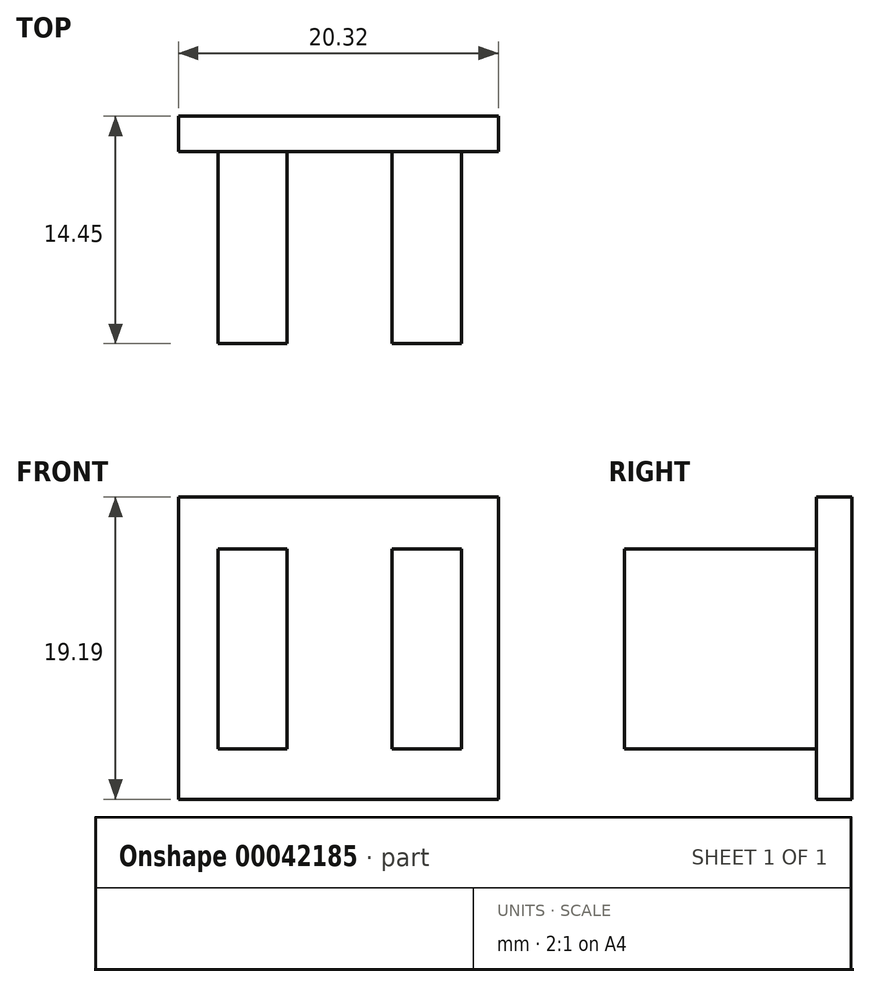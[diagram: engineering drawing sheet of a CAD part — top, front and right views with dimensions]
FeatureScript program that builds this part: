
annotation { "Feature Type Name" : "Feature", "Feature Type Description" : "" }
export const myFeature = defineFeature(function(context is Context, id is Id, definition is map)
    precondition{}
    {
        {
            var Q0;
            Q0=qCreatedBy(makeId("Front.planeOp"),FACE);
            var sketch = newSketch(context, id + "F0", { "sketchPlane" : qUnion([Q0])});
            skLineSegment(sketch, "E0.rect.bottom", {"start": v(0, 1.86) * mm, "end": v(-20.32, 1.86) * mm});
            skLineSegment(sketch, "E0.rect.top", {"start": v(0, 21.05) * mm, "end": v(-20.32, 21.05) * mm});
            skLineSegment(sketch, "E0.rect.left", {"start": v(0, 1.86) * mm, "end": v(0, 21.05) * mm});
            skLineSegment(sketch, "E0.rect.right", {"start": v(-20.32, 1.86) * mm, "end": v(-20.32, 21.05) * mm});
            skPoint(sketch, "E0.rect.middle", {"position": v(-10.16, 11.45) * mm});
            skSolve(sketch);
        }
        {
            var Q0;
            Q0 = qSketchRegion(id + "F0", true);
            extrude(context, id + "F1", {"entities" : qUnion([Q0]), "depth" : 2.26 * mm});
        }
        {
            var Q0;
            Q0=makeQuery(id+"F1.opExtrude","CAP_FACE",FACE,{"disambiguationData":[OSD([sQuery(id+"F0.wireOp",EDGE,"E0.rect.bottom"),sQuery(id+"F0.wireOp",EDGE,"E0.rect.top"),sQuery(id+"F0.wireOp",EDGE,"E0.rect.left"),sQuery(id+"F0.wireOp",EDGE,"E0.rect.right")])],"isStart":false});
            var sketch = newSketch(context, id + "F2", { "sketchPlane" : qUnion([Q0])});
            skLineSegment(sketch, "E1.rect.bottom", {"start": v(-13.42, 5.05) * mm, "end": v(-17.81, 5.05) * mm});
            skLineSegment(sketch, "E1.rect.top", {"start": v(-13.42, 17.75) * mm, "end": v(-17.81, 17.75) * mm});
            skLineSegment(sketch, "E1.rect.left", {"start": v(-13.42, 5.05) * mm, "end": v(-13.42, 17.75) * mm});
            skLineSegment(sketch, "E1.rect.right", {"start": v(-17.81, 5.05) * mm, "end": v(-17.81, 17.75) * mm});
            skPoint(sketch, "E1.rect.middle", {"position": v(-15.61, 11.4) * mm});
            skLineSegment(sketch, "E2", {"start": v(-10.08, -6.85) * mm, "end": v(-10.08, 35.98) * mm, "construction": true});
            skLineSegment(sketch, "E3.MirrorCS", {"start": v(-6.74, 5.05) * mm, "end": v(-2.35, 5.05) * mm});
            skPoint(sketch, "E4.MirrorP", {"position": v(-4.55, 11.4) * mm});
            skLineSegment(sketch, "E5.MirrorCS", {"start": v(-6.74, 5.05) * mm, "end": v(-6.74, 17.75) * mm});
            skLineSegment(sketch, "E6.MirrorCS", {"start": v(-6.74, 17.75) * mm, "end": v(-2.35, 17.75) * mm});
            skLineSegment(sketch, "E7.MirrorCS", {"start": v(-2.35, 5.05) * mm, "end": v(-2.35, 17.75) * mm});
            skSolve(sketch);
        }
        {
            var Q0;
            Q0 = qSketchRegion(id + "F2", true);
            var Q1;
            Q1=sQuery(id+"F2.wireOp",EDGE,"E1.rect.top");
            var Q2;
            Q2=sQuery(id+"F2.wireOp",EDGE,"E1.rect.bottom");
            var Q3;
            Q3=sQuery(id+"F2.wireOp",EDGE,"E1.rect.right");
            var Q4;
            Q4=sQuery(id+"F2.wireOp",EDGE,"E1.rect.left");
            extrude(context, id + "F3", {"entities" : qUnion([Q0]), "operationType" : NewBodyOperationType.ADD, "surfaceEntities" : qUnion([Q1, Q2, Q3, Q4]), "depth" : 12.2 * mm});
        }
    });
